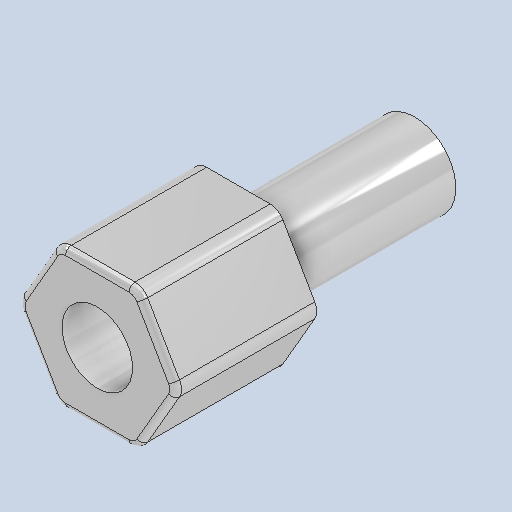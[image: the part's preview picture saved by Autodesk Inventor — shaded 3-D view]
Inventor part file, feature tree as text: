
AUTODESK INVENTOR PART (.ipt)
format: ipt  version: 2024.2 (Build 282272000, 272)  size: 172,544 bytes
history: native  units: mm
features: extrude x3, fillet x2, sketch x1
ambient origin geometry x8: Origin, YZ Plane, XZ Plane, XY Plane, X Axis, Y Axis, Z Axis, Center Point
bodies: Solid1 (feature_tree)
feature tree (6):
  extrude  "Extrusion1"  Depth=4.8mm TaperAngle=0.0deg
  extrude  "Extrusion2"  Depth=0.2mm
  extrude  "Extrusion3"  Depth=6.0mm TaperAngle=0.0deg
  fillet  "Fillet1"  Radius=2.4mm
  fillet  "Fillet2"  Radius=4.0mm
  sketch  "Sketch1"  dims[d0=4.75mm d1=4.8mm d2=0.0mm d3=2.8mm d4=6.0mm d5=0.0mm d6=2.4mm d7=4.0mm d8=0.0mm d9=0.5mm d10=0.2mm]
